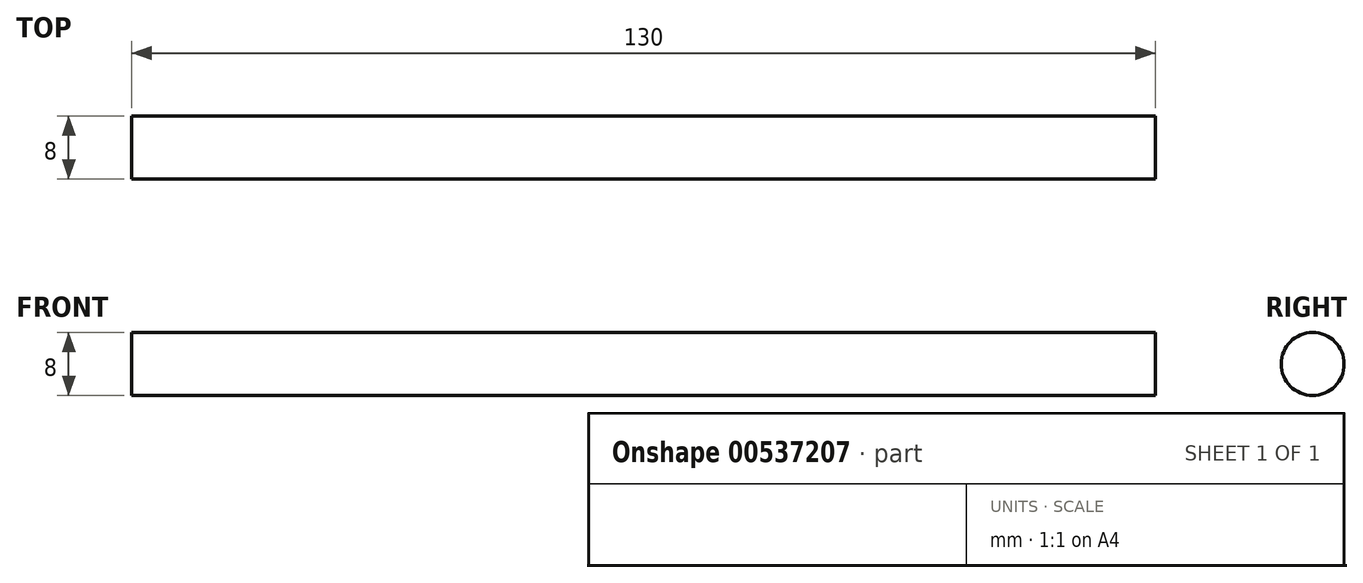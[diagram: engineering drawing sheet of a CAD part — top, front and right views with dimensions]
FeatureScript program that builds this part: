
annotation { "Feature Type Name" : "Feature", "Feature Type Description" : "" }
export const myFeature = defineFeature(function(context is Context, id is Id, definition is map)
    precondition{}
    {
        {
            var Q0;
            Q0=qCreatedBy(makeId("Right.planeOp"),FACE);
            var sketch = newSketch(context, id + "F0", { "sketchPlane" : qUnion([Q0])});
            skCircle(sketch, "E0", {"center": v(0, 0) * mm, "radius": 4 * mm});
            skSolve(sketch);
        }
        {
            var Q0;
            Q0=makeQuery(id+"F0.imprint","IMPRINT",FACE,{"disambiguationData":[TD([[makeQuery(id+"F0.imprint","IMPRINT",EDGE,{"derivedFrom":sQuery(id+"F0.wireOp",EDGE,"E0")}),1.0]])]});
            extrude(context, id + "F1", {"entities" : qUnion([Q0]), "endBound" : BoundingType.SYMMETRIC, "depth" : 130 * mm, "offsetDistance" : 25 * mm});
        }
    });
